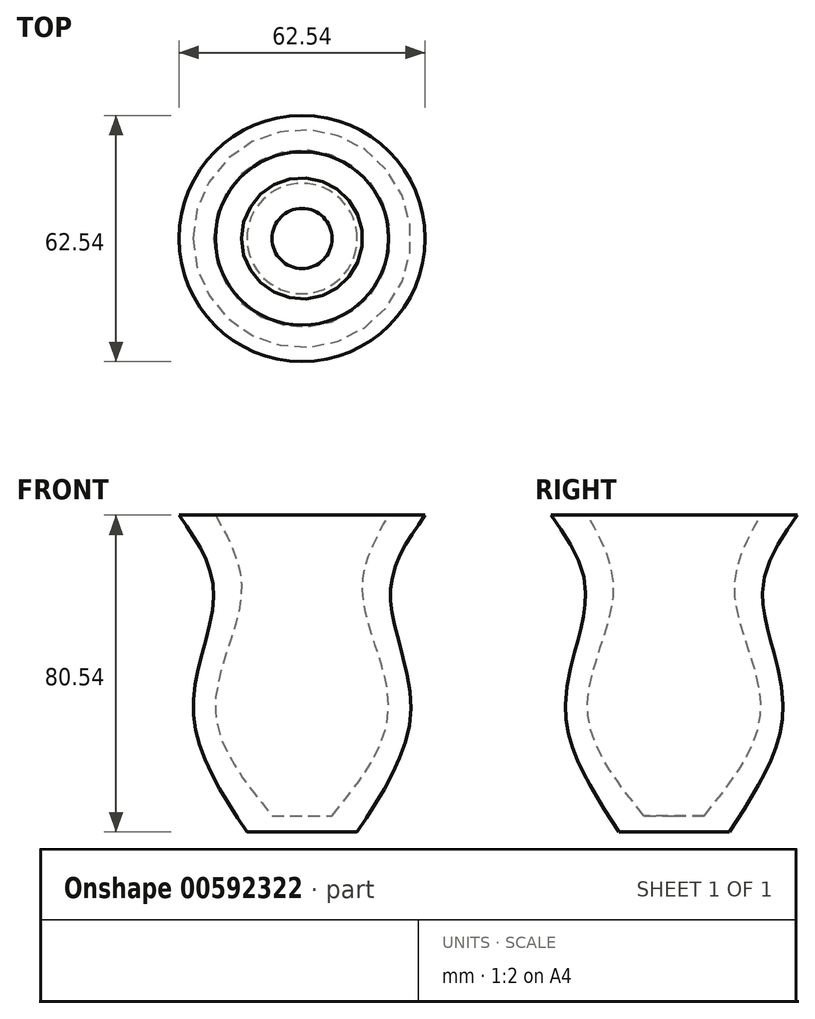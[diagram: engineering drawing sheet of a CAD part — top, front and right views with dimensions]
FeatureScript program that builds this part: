
annotation { "Feature Type Name" : "Feature", "Feature Type Description" : "" }
export const myFeature = defineFeature(function(context is Context, id is Id, definition is map)
    precondition{}
    {
        {
            var Q0;
            Q0=qCreatedBy(makeId("Front.planeOp"),FACE);
            var sketch = newSketch(context, id + "F0", { "sketchPlane" : qUnion([Q0])});
            skLineSegment(sketch, "E0", {"start": v(0, 0) * mm, "end": v(0, 4.17) * mm, "construction": true});
            skLineSegment(sketch, "E1", {"start": v(0, 0) * mm, "end": v(14.01, 0) * mm});
            skLineSegment(sketch, "E2", {"start": v(0, 0) * mm, "end": v(0, 7.22) * mm});
            skFitSpline(sketch, "E3", {"points": [v(14.01, 0) * mm, v(27.66, 31.4) * mm, v(22.48, 60.8) * mm, v(31.27, 80.54) * mm], "startDerivative": vector(55.12, 84.26) * mm, "endDerivative": vector(44.44, 63.33) * mm});
            skLineSegment(sketch, "E4", {"start": v(31.27, 80.54) * mm, "end": v(22.02, 80.54) * mm});
            skLineSegment(sketch, "E5", {"start": v(7.64, 4.17) * mm, "end": v(0, 4.17) * mm});
            skLineSegment(sketch, "E6.trimOffspring", {"start": v(0, 7.22) * mm, "end": v(0, 103.8) * mm, "construction": true});
            skFitSpline(sketch, "E7", {"points": [v(22.02, 80.54) * mm, v(15.42, 60.37) * mm, v(22.02, 31.26) * mm, v(7.64, 4.17) * mm], "startDerivative": vector(-36.1, -64.3) * mm, "endDerivative": vector(-59.58, -73.43) * mm});
            skSolve(sketch);
        }
        {
            var Q0;
            {var subQ1=sQuery(id+"F0.wireOp",EDGE,"E1");Q0=makeQuery(id+"F0.imprint","IMPRINT",FACE,{"disambiguationData":[TD([[makeQuery(id+"F0.imprint","IMPRINT",EDGE,{"derivedFrom":subQ1}),1.0]])]});}
            var Q1;
            Q1=sQuery(id+"F0.wireOp",EDGE,"E6.trimOffspring");
            revolve(context, id + "F1", {"entities" : qUnion([Q0]), "axis" : qUnion([Q1]), "revolveType" : RevolveType.FULL});
        }
    });
